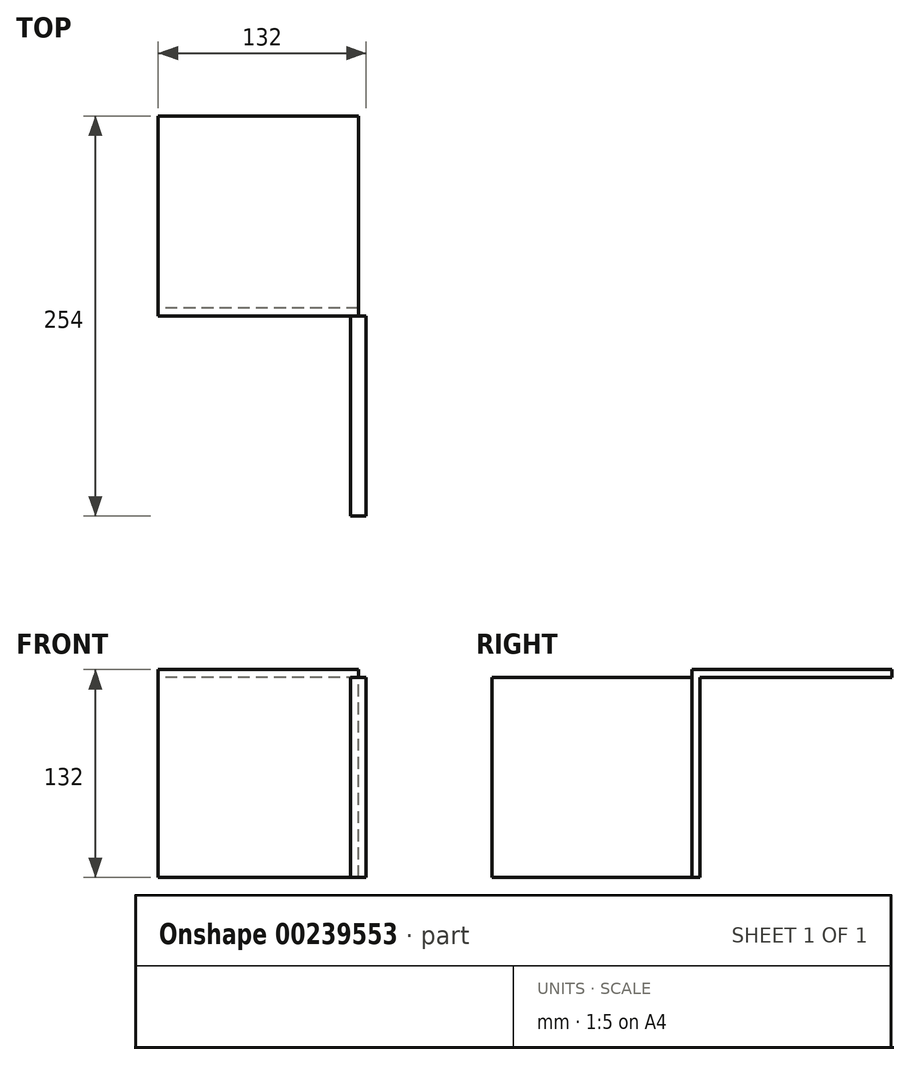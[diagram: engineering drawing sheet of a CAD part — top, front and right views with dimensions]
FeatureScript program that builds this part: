
annotation { "Feature Type Name" : "Feature", "Feature Type Description" : "" }
export const myFeature = defineFeature(function(context is Context, id is Id, definition is map)
    precondition{}
    {
        {
            assignVariable(context, id + "F0", {"name" : "L", "anyValue" : 5});
        }
        {
            var Q0;
            Q0=qCreatedBy(makeId("Right.planeOp"),FACE);
            var sketch = newSketch(context, id + "F1", { "sketchPlane" : qUnion([Q0])});
            skLineSegment(sketch, "E0.bottom", {"start": v(63.5, 63.5) * mm, "end": v(-63.5, 63.5) * mm});
            skLineSegment(sketch, "E0.top", {"start": v(63.5, -63.5) * mm, "end": v(-63.5, -63.5) * mm});
            skLineSegment(sketch, "E0.left", {"start": v(63.5, 63.5) * mm, "end": v(63.5, -63.5) * mm});
            skLineSegment(sketch, "E0.right", {"start": v(-63.5, 63.5) * mm, "end": v(-63.5, -63.5) * mm});
            skPoint(sketch, "E0.middle", {"position": v(0, 0) * mm});
            skSolve(sketch);
        }
        {
            var Q0;
            Q0 = qSketchRegion(id + "F1", true);
            extrude(context, id + "F2", {"entities" : qUnion([Q0]), "endBound" : BoundingType.SYMMETRIC, "depth" : (getVariable(context, 'L') * 2) * mm});
        }
        {
            var Q0;
            Q0=makeQuery(id+"F2.opExtrude","SWEPT_FACE",FACE,{"disambiguationData":[OSD([sQuery(id+"F1.wireOp",EDGE,"E0.left")])]});
            var sketch = newSketch(context, id + "F3", { "sketchPlane" : qUnion([Q0])});
            skLineSegment(sketch, "E1.bottom", {"start": v(0, -63.5) * mm, "end": v(127, -63.5) * mm});
            skLineSegment(sketch, "E1.top", {"start": v(0, 63.5) * mm, "end": v(127, 63.5) * mm});
            skLineSegment(sketch, "E1.left", {"start": v(0, -63.5) * mm, "end": v(0, 63.5) * mm});
            skLineSegment(sketch, "E1.right", {"start": v(127, -63.5) * mm, "end": v(127, 63.5) * mm});
            skSolve(sketch);
        }
        {
            var Q0;
            Q0 = qSketchRegion(id + "F3", true);
            extrude(context, id + "F4", {"entities" : qUnion([Q0]), "operationType" : NewBodyOperationType.ADD, "depth" : (getVariable(context, 'L')) * mm});
        }
        {
            var Q0;
            Q0=makeQuery(id+"F4.boolean.opBoolean","MERGE",FACE,{"derivedFrom":[makeQuery(id+"F2.opExtrude","SWEPT_FACE",FACE,{"disambiguationData":[OSD([sQuery(id+"F1.wireOp",EDGE,"E0.bottom")])]}),makeQuery(id+"F4.opExtrude","SWEPT_FACE",FACE,{"disambiguationData":[OSD([sQuery(id+"F3.wireOp",EDGE,"E1.top")])]})]});
            var sketch = newSketch(context, id + "F5", { "sketchPlane" : qUnion([Q0])});
            skLineSegment(sketch, "E2.bottom", {"start": v(0, 63.5) * mm, "end": v(-127, 63.5) * mm});
            skLineSegment(sketch, "E2.top", {"start": v(0, 190.5) * mm, "end": v(-127, 190.5) * mm});
            skLineSegment(sketch, "E2.left", {"start": v(0, 63.5) * mm, "end": v(0, 190.5) * mm});
            skLineSegment(sketch, "E2.right", {"start": v(-127, 63.5) * mm, "end": v(-127, 190.5) * mm});
            skSolve(sketch);
        }
        {
            var Q0;
            Q0 = qSketchRegion(id + "F5", true);
            extrude(context, id + "F6", {"entities" : qUnion([Q0]), "operationType" : NewBodyOperationType.ADD, "depth" : (getVariable(context, 'L')) * mm});
        }
    });
